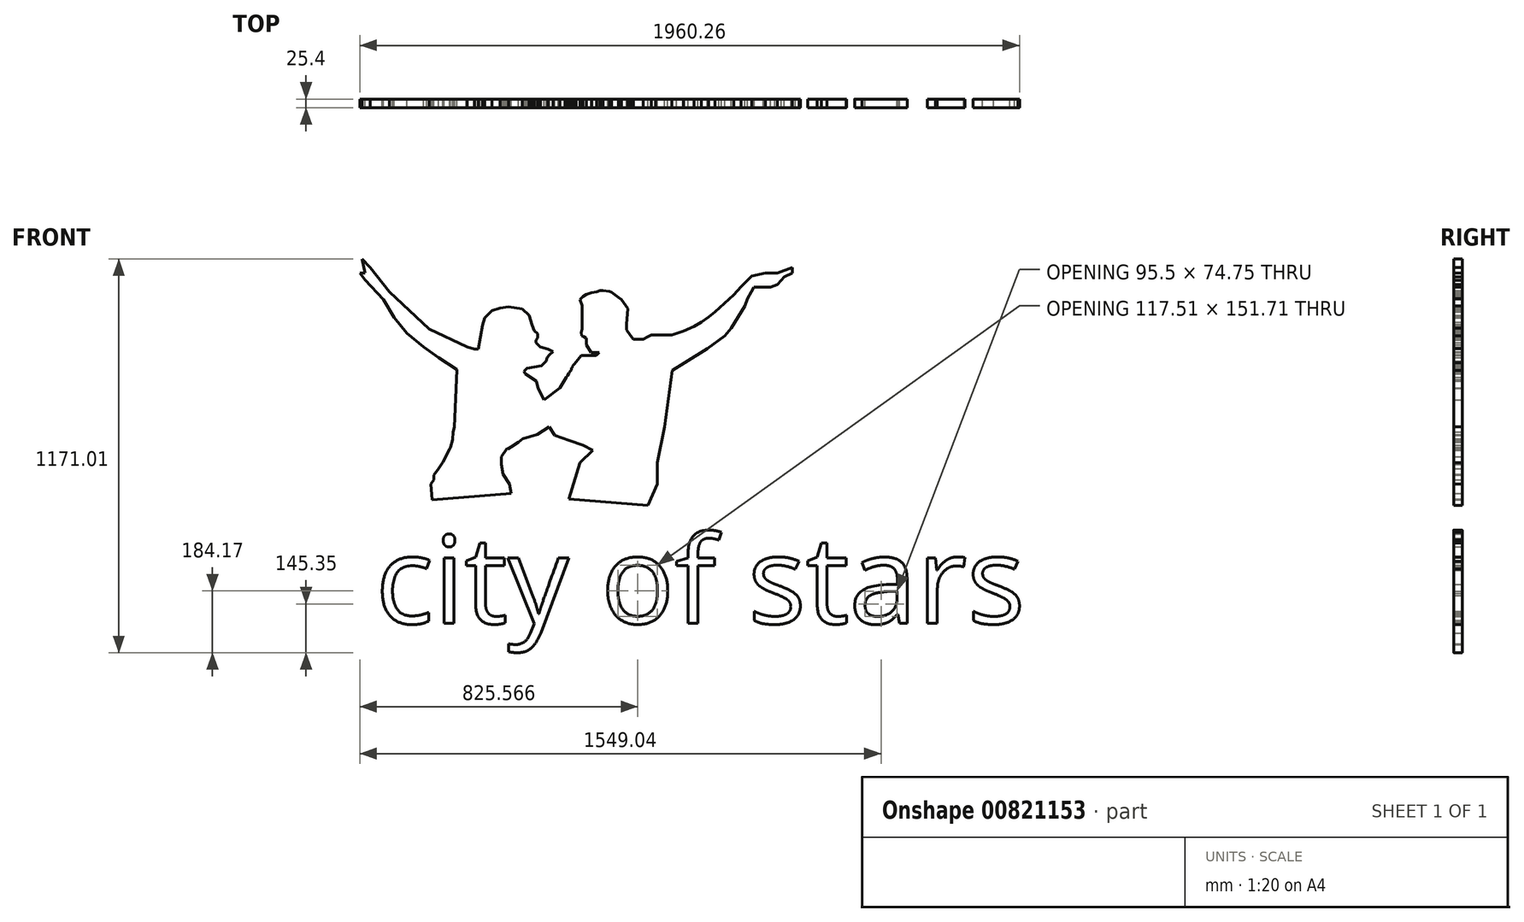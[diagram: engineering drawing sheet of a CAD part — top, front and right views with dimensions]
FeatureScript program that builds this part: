
annotation { "Feature Type Name" : "Feature", "Feature Type Description" : "" }
export const myFeature = defineFeature(function(context is Context, id is Id, definition is map)
    precondition{}
    {
        {
            var Q0;
            Q0=qCreatedBy(makeId("Front.planeOp"),FACE);
            var sketch = newSketch(context, id + "F0", { "sketchPlane" : qUnion([Q0])});
            skLineSegment(sketch, "E0", {"start": v(-24.6, -208.57) * mm, "end": v(-79.3, -173.4) * mm});
            skLineSegment(sketch, "E1", {"start": v(-79.3, -173.4) * mm, "end": v(-123.58, -142.15) * mm});
            skLineSegment(sketch, "E2", {"start": v(-123.58, -142.15) * mm, "end": v(-173.07, -100.48) * mm});
            skLineSegment(sketch, "E3", {"start": v(-173.07, -100.48) * mm, "end": v(-212.13, -53.6) * mm});
            skLineSegment(sketch, "E4", {"start": v(-212.13, -53.6) * mm, "end": v(-243.39, 0) * mm});
            skLineSegment(sketch, "E5", {"start": v(-243.39, 0) * mm, "end": v(-298.08, 58.4) * mm});
            skLineSegment(sketch, "E6", {"start": v(-298.08, 58.4) * mm, "end": v(-313.15, 78.62) * mm});
            skLineSegment(sketch, "E7", {"start": v(-313.15, 78.62) * mm, "end": v(-298.41, 78.62) * mm});
            skLineSegment(sketch, "E8", {"start": v(-298.41, 78.62) * mm, "end": v(-306.72, 120.17) * mm});
            skLineSegment(sketch, "E9", {"start": v(-306.72, 120.17) * mm, "end": v(-282.38, 94.19) * mm});
            skLineSegment(sketch, "E10", {"start": v(-282.38, 94.19) * mm, "end": v(-225.5, 22.33) * mm});
            skLineSegment(sketch, "E11", {"start": v(-225.5, 22.33) * mm, "end": v(-177.52, -22.63) * mm});
            skLineSegment(sketch, "E12", {"start": v(-177.52, -22.63) * mm, "end": v(-131.04, -66.18) * mm});
            skLineSegment(sketch, "E13", {"start": v(-131.04, -66.18) * mm, "end": v(-107.71, -88.04) * mm});
            skLineSegment(sketch, "E14", {"start": v(-107.71, -88.04) * mm, "end": v(4.94, -141.63) * mm});
            skLineSegment(sketch, "E15", {"start": v(4.94, -141.63) * mm, "end": v(26.85, -148.43) * mm});
            skLineSegment(sketch, "E16", {"start": v(26.85, -148.43) * mm, "end": v(38.19, -148.43) * mm});
            skLineSegment(sketch, "E17", {"start": v(38.19, -148.43) * mm, "end": v(51.4, -76.65) * mm});
            skLineSegment(sketch, "E18", {"start": v(51.4, -76.65) * mm, "end": v(58.06, -55.21) * mm});
            skLineSegment(sketch, "E19", {"start": v(58.06, -55.21) * mm, "end": v(78.67, -33.22) * mm});
            skLineSegment(sketch, "E20", {"start": v(78.67, -33.22) * mm, "end": v(102.79, -25.65) * mm});
            skLineSegment(sketch, "E21", {"start": v(102.79, -25.65) * mm, "end": v(128.88, -22.63) * mm});
            skLineSegment(sketch, "E22", {"start": v(128.88, -22.63) * mm, "end": v(168.72, -28.06) * mm});
            skLineSegment(sketch, "E23", {"start": v(168.72, -28.06) * mm, "end": v(189.58, -47.6) * mm});
            skLineSegment(sketch, "E24", {"start": v(189.58, -47.6) * mm, "end": v(198.86, -76.65) * mm});
            skLineSegment(sketch, "E25", {"start": v(198.86, -76.65) * mm, "end": v(205, -92.93) * mm});
            skLineSegment(sketch, "E26", {"start": v(205, -92.93) * mm, "end": v(215.26, -102.55) * mm});
            skLineSegment(sketch, "E27", {"start": v(215.26, -102.55) * mm, "end": v(215.26, -115.4) * mm});
            skLineSegment(sketch, "E28", {"start": v(215.26, -115.4) * mm, "end": v(209.33, -120.96) * mm});
            skLineSegment(sketch, "E29", {"start": v(209.33, -120.96) * mm, "end": v(209.33, -129.2) * mm});
            skLineSegment(sketch, "E30", {"start": v(209.33, -129.2) * mm, "end": v(222.04, -141.11) * mm});
            skLineSegment(sketch, "E31", {"start": v(222.04, -141.11) * mm, "end": v(245.6, -148.43) * mm});
            skLineSegment(sketch, "E32", {"start": v(245.6, -148.43) * mm, "end": v(260.68, -155.6) * mm});
            skLineSegment(sketch, "E33", {"start": v(260.68, -155.6) * mm, "end": v(251, -164.66) * mm});
            skLineSegment(sketch, "E34", {"start": v(251, -164.66) * mm, "end": v(243.5, -172.67) * mm});
            skLineSegment(sketch, "E35", {"start": v(243.5, -172.67) * mm, "end": v(240.24, -182.84) * mm});
            skLineSegment(sketch, "E36", {"start": v(240.24, -182.84) * mm, "end": v(226.73, -197.25) * mm});
            skLineSegment(sketch, "E37", {"start": v(226.73, -197.25) * mm, "end": v(183.54, -204.8) * mm});
            skLineSegment(sketch, "E38", {"start": v(183.54, -204.8) * mm, "end": v(174.41, -214.54) * mm});
            skLineSegment(sketch, "E39", {"start": v(174.41, -214.54) * mm, "end": v(178.43, -221.66) * mm});
            skLineSegment(sketch, "E40", {"start": v(178.43, -221.66) * mm, "end": v(211.63, -243.62) * mm});
            skLineSegment(sketch, "E41", {"start": v(211.63, -243.62) * mm, "end": v(216.23, -264.57) * mm});
            skLineSegment(sketch, "E42", {"start": v(216.23, -264.57) * mm, "end": v(234.62, -298.8) * mm});
            skLineSegment(sketch, "E43", {"start": v(234.62, -298.8) * mm, "end": v(280.6, -264.06) * mm});
            skLineSegment(sketch, "E44", {"start": v(280.6, -264.06) * mm, "end": v(296.94, -238) * mm});
            skLineSegment(sketch, "E45", {"start": v(296.94, -238) * mm, "end": v(300, -231.87) * mm});
            skLineSegment(sketch, "E46", {"start": v(300, -231.87) * mm, "end": v(303.58, -226.26) * mm});
            skLineSegment(sketch, "E47", {"start": v(303.58, -226.26) * mm, "end": v(307.15, -220.64) * mm});
            skLineSegment(sketch, "E48", {"start": v(307.15, -220.64) * mm, "end": v(309.2, -217.57) * mm});
            skLineSegment(sketch, "E49", {"start": v(309.2, -217.57) * mm, "end": v(311.75, -213.49) * mm});
            skLineSegment(sketch, "E50", {"start": v(311.75, -213.49) * mm, "end": v(314.82, -209.9) * mm});
            skLineSegment(sketch, "E51", {"start": v(314.82, -209.9) * mm, "end": v(314.82, -203.27) * mm});
            skLineSegment(sketch, "E52", {"start": v(314.82, -203.27) * mm, "end": v(317.37, -203.27) * mm});
            skLineSegment(sketch, "E53", {"start": v(318.4, -199.7) * mm, "end": v(321.97, -195.1) * mm});
            skLineSegment(sketch, "E54", {"start": v(321.97, -195.1) * mm, "end": v(324.01, -192.54) * mm});
            skLineSegment(sketch, "E55", {"start": v(324.01, -192.54) * mm, "end": v(329.12, -185.4) * mm});
            skLineSegment(sketch, "E56", {"start": v(329.12, -185.4) * mm, "end": v(344.95, -167.51) * mm});
            skLineSegment(sketch, "E57", {"start": v(344.95, -167.51) * mm, "end": v(388.56, -167.51) * mm});
            skLineSegment(sketch, "E58", {"start": v(388.56, -167.51) * mm, "end": v(397.42, -158.06) * mm});
            skLineSegment(sketch, "E59", {"start": v(397.42, -158.06) * mm, "end": v(373.8, -158.06) * mm});
            skLineSegment(sketch, "E60", {"start": v(373.8, -158.06) * mm, "end": v(359.75, -134.75) * mm});
            skLineSegment(sketch, "E61", {"start": v(359.75, -134.75) * mm, "end": v(359.75, -118.95) * mm});
            skLineSegment(sketch, "E62", {"start": v(359.75, -118.95) * mm, "end": v(358.48, -114.43) * mm});
            skLineSegment(sketch, "E63", {"start": v(358.48, -114.43) * mm, "end": v(352.73, -111.28) * mm});
            skLineSegment(sketch, "E64", {"start": v(346.35, -108.57) * mm, "end": v(344.95, -97.73) * mm});
            skLineSegment(sketch, "E65", {"start": v(344.95, -97.73) * mm, "end": v(346.99, -87.8) * mm});
            skLineSegment(sketch, "E66", {"start": v(346.99, -87.8) * mm, "end": v(346.99, -61.17) * mm});
            skLineSegment(sketch, "E67", {"start": v(352.73, -111.28) * mm, "end": v(346.35, -108.57) * mm});
            skLineSegment(sketch, "E68", {"start": v(346.99, -61.17) * mm, "end": v(346.99, -34) * mm});
            skLineSegment(sketch, "E69", {"start": v(346.99, -34) * mm, "end": v(346.99, -18.52) * mm});
            skLineSegment(sketch, "E70", {"start": v(346.99, -18.52) * mm, "end": v(341.37, 0) * mm});
            skLineSegment(sketch, "E71", {"start": v(341.37, 0) * mm, "end": v(350.3, 7.7) * mm});
            skLineSegment(sketch, "E72", {"start": v(350.3, 7.7) * mm, "end": v(360.05, 14.94) * mm});
            skLineSegment(sketch, "E73", {"start": v(360.05, 14.94) * mm, "end": v(375, 20.23) * mm});
            skLineSegment(sketch, "E74", {"start": v(375, 20.23) * mm, "end": v(389.68, 22.88) * mm});
            skLineSegment(sketch, "E75", {"start": v(389.68, 22.88) * mm, "end": v(400.6, 25.52) * mm});
            skLineSegment(sketch, "E76", {"start": v(400.6, 25.52) * mm, "end": v(404.92, 26.13) * mm});
            skLineSegment(sketch, "E77", {"start": v(404.92, 26.13) * mm, "end": v(409.24, 26.13) * mm});
            skLineSegment(sketch, "E78", {"start": v(409.24, 26.13) * mm, "end": v(428.22, 23.7) * mm});
            skLineSegment(sketch, "E79", {"start": v(428.22, 23.7) * mm, "end": v(434.84, 21.25) * mm});
            skLineSegment(sketch, "E80", {"start": v(434.84, 21.25) * mm, "end": v(454.69, 5.59) * mm});
            skLineSegment(sketch, "E81", {"start": v(454.69, 5.59) * mm, "end": v(464.18, -0.1) * mm});
            skLineSegment(sketch, "E82", {"start": v(464.18, -0.1) * mm, "end": v(482.59, -27.77) * mm});
            skLineSegment(sketch, "E83", {"start": v(482.59, -27.77) * mm, "end": v(479.14, -74.15) * mm});
            skLineSegment(sketch, "E84", {"start": v(479.14, -74.15) * mm, "end": v(479.14, -91.15) * mm});
            skLineSegment(sketch, "E85", {"start": v(479.14, -91.15) * mm, "end": v(490, -106.9) * mm});
            skLineSegment(sketch, "E86", {"start": v(490, -106.9) * mm, "end": v(498.9, -118.11) * mm});
            skLineSegment(sketch, "E87", {"start": v(498.9, -118.11) * mm, "end": v(529.23, -118.11) * mm});
            skLineSegment(sketch, "E88", {"start": v(529.23, -118.11) * mm, "end": v(543.15, -111.03) * mm});
            skLineSegment(sketch, "E89", {"start": v(543.15, -111.03) * mm, "end": v(553.44, -105.72) * mm});
            skLineSegment(sketch, "E90", {"start": v(553.44, -105.72) * mm, "end": v(565.68, -106.11) * mm});
            skLineSegment(sketch, "E91", {"start": v(565.68, -106.11) * mm, "end": v(613.7, -106.11) * mm});
            skLineSegment(sketch, "E92", {"start": v(613.7, -106.11) * mm, "end": v(648.53, -93.94) * mm});
            skLineSegment(sketch, "E93", {"start": v(648.53, -93.94) * mm, "end": v(680.26, -80.8) * mm});
            skLineSegment(sketch, "E94", {"start": v(680.26, -80.8) * mm, "end": v(701.15, -68.22) * mm});
            skLineSegment(sketch, "E95", {"start": v(701.15, -68.22) * mm, "end": v(723.6, -52.9) * mm});
            skLineSegment(sketch, "E96", {"start": v(723.6, -52.9) * mm, "end": v(742.17, -37.03) * mm});
            skLineSegment(sketch, "E97", {"start": v(742.17, -37.03) * mm, "end": v(797.89, 13.31) * mm});
            skLineSegment(sketch, "E98", {"start": v(797.89, 13.31) * mm, "end": v(819.55, 37.39) * mm});
            skLineSegment(sketch, "E99", {"start": v(819.55, 37.39) * mm, "end": v(851.28, 69.67) * mm});
            skLineSegment(sketch, "E100", {"start": v(851.28, 69.67) * mm, "end": v(891.52, 77.88) * mm});
            skLineSegment(sketch, "E101", {"start": v(891.52, 77.88) * mm, "end": v(927.12, 77.88) * mm});
            skLineSegment(sketch, "E102", {"start": v(927.12, 77.88) * mm, "end": v(972, 94.84) * mm});
            skLineSegment(sketch, "E103", {"start": v(972, 94.84) * mm, "end": v(972, 77.88) * mm});
            skLineSegment(sketch, "E104", {"start": v(972, 77.88) * mm, "end": v(947.24, 66.39) * mm});
            skLineSegment(sketch, "E105", {"start": v(947.24, 66.39) * mm, "end": v(938.73, 56) * mm});
            skLineSegment(sketch, "E106", {"start": v(938.73, 56) * mm, "end": v(927.12, 44.5) * mm});
            skLineSegment(sketch, "E107", {"start": v(927.12, 44.5) * mm, "end": v(907, 36.84) * mm});
            skLineSegment(sketch, "E108", {"start": v(907, 36.84) * mm, "end": v(857.47, 36.84) * mm});
            skLineSegment(sketch, "E109", {"start": v(857.47, 36.84) * mm, "end": v(849.74, 22.07) * mm});
            skLineSegment(sketch, "E110", {"start": v(849.74, 22.07) * mm, "end": v(838.9, 1.82) * mm});
            skLineSegment(sketch, "E111", {"start": v(838.9, 1.82) * mm, "end": v(830.39, -18.98) * mm});
            skLineSegment(sketch, "E112", {"start": v(830.39, -18.98) * mm, "end": v(790.15, -85.73) * mm});
            skLineSegment(sketch, "E113", {"start": v(790.15, -85.73) * mm, "end": v(770.8, -108.72) * mm});
            skLineSegment(sketch, "E114", {"start": v(770.8, -108.72) * mm, "end": v(719.72, -147.02) * mm});
            skLineSegment(sketch, "E115", {"start": v(719.72, -147.02) * mm, "end": v(651.62, -188.61) * mm});
            skLineSegment(sketch, "E116", {"start": v(651.62, -188.61) * mm, "end": v(631.5, -201.2) * mm});
            skLineSegment(sketch, "E117", {"start": v(631.5, -201.2) * mm, "end": v(614.78, -211.65) * mm});
            skLineSegment(sketch, "E118", {"start": v(614.78, -211.65) * mm, "end": v(592.04, -379.59) * mm});
            skLineSegment(sketch, "E119", {"start": v(592.04, -379.59) * mm, "end": v(571.14, -485.2) * mm});
            skLineSegment(sketch, "E120", {"start": v(571.14, -485.2) * mm, "end": v(571.14, -548.62) * mm});
            skLineSegment(sketch, "E121", {"start": v(571.14, -548.62) * mm, "end": v(542.3, -612.08) * mm});
            skLineSegment(sketch, "E122", {"start": v(542.3, -612.08) * mm, "end": v(308.03, -593.8) * mm});
            skLineSegment(sketch, "E123", {"start": v(308.03, -593.8) * mm, "end": v(340.74, -485.2) * mm});
            skLineSegment(sketch, "E124", {"start": v(340.74, -485.2) * mm, "end": v(378.77, -448.59) * mm});
            skLineSegment(sketch, "E125", {"start": v(378.77, -448.59) * mm, "end": v(350.3, -434.07) * mm});
            skLineSegment(sketch, "E126", {"start": v(350.3, -434.07) * mm, "end": v(308.8, -419.55) * mm});
            skLineSegment(sketch, "E127", {"start": v(308.8, -419.55) * mm, "end": v(265.44, -405.03) * mm});
            skLineSegment(sketch, "E128", {"start": v(265.44, -405.03) * mm, "end": v(249.53, -379.59) * mm});
            skLineSegment(sketch, "E129", {"start": v(249.53, -379.59) * mm, "end": v(213.56, -402.08) * mm});
            skLineSegment(sketch, "E130", {"start": v(213.56, -402.08) * mm, "end": v(171.13, -414.7) * mm});
            skLineSegment(sketch, "E131", {"start": v(171.13, -414.7) * mm, "end": v(158.2, -424.93) * mm});
            skLineSegment(sketch, "E132", {"start": v(158.2, -424.93) * mm, "end": v(135.7, -439) * mm});
            skLineSegment(sketch, "E133", {"start": v(135.7, -439) * mm, "end": v(126.26, -444.82) * mm});
            skLineSegment(sketch, "E134", {"start": v(126.26, -444.82) * mm, "end": v(123.21, -443.75) * mm});
            skLineSegment(sketch, "E135", {"start": v(123.21, -443.75) * mm, "end": v(107.24, -467.95) * mm});
            skLineSegment(sketch, "E136", {"start": v(107.24, -467.95) * mm, "end": v(107.24, -491.08) * mm});
            skLineSegment(sketch, "E137", {"start": v(107.24, -491.08) * mm, "end": v(112.68, -519.39) * mm});
            skLineSegment(sketch, "E138", {"start": v(112.68, -519.39) * mm, "end": v(131.29, -549.13) * mm});
            skLineSegment(sketch, "E139", {"start": v(131.29, -549.13) * mm, "end": v(136.23, -576.73) * mm});
            skLineSegment(sketch, "E140", {"start": v(136.23, -576.73) * mm, "end": v(-98.5, -596.66) * mm});
            skLineSegment(sketch, "E141", {"start": v(-98.5, -596.66) * mm, "end": v(-102.54, -549.13) * mm});
            skLineSegment(sketch, "E142", {"start": v(-102.54, -549.13) * mm, "end": v(-93.56, -536.85) * mm});
            skLineSegment(sketch, "E143", {"start": v(-93.56, -536.85) * mm, "end": v(-93.56, -521.9) * mm});
            skLineSegment(sketch, "E144", {"start": v(-93.56, -521.9) * mm, "end": v(-79.47, -503.46) * mm});
            skLineSegment(sketch, "E145", {"start": v(-79.47, -503.46) * mm, "end": v(-67.48, -484.52) * mm});
            skLineSegment(sketch, "E146", {"start": v(-67.48, -484.52) * mm, "end": v(-46.34, -444.64) * mm});
            skLineSegment(sketch, "E147", {"start": v(-43.52, -440.16) * mm, "end": v(-37.17, -417.23) * mm});
            skLineSegment(sketch, "E148", {"start": v(-37.17, -417.23) * mm, "end": v(-36.47, -393.8) * mm});
            skLineSegment(sketch, "E149", {"start": v(-36.47, -393.8) * mm, "end": v(-32.24, -379.85) * mm});
            skLineSegment(sketch, "E150", {"start": v(-43.52, -440.16) * mm, "end": v(-46.34, -444.64) * mm});
            skLineSegment(sketch, "E151", {"start": v(-32.24, -379.85) * mm, "end": v(-24.6, -208.57) * mm});
            skLineSegment(sketch, "E152", {"start": v(317.37, -203.27) * mm, "end": v(318.4, -199.7) * mm});
            skSolve(sketch);
        }
        {
            var Q0;
            Q0 = qSketchRegion(id + "F0", true);
            extrude(context, id + "F1", {"entities" : qUnion([Q0]), "depth" : 25.4 * mm, "offsetDistance" : 25.4 * mm});
        }
        {
            var Q0;
            Q0=qCreatedBy(makeId("Front.planeOp"),FACE);
            var sketch = newSketch(context, id + "F2", { "sketchPlane" : qUnion([Q0])});
            skText(sketch, "E153", { "text": "city of stars\n", "fontName": "OpenSans-Regular.ttf"});
            const initialGuessF2  = {"E153": [-0.26715, -0.96362, 1, 0, 0.26133]};
            skSetInitialGuess(sketch, initialGuessF2);
            skSolve(sketch);
        }
        {
            var Q0;
            Q0 = qSketchRegion(id + "F2", true);
            extrude(context, id + "F3", {"entities" : qUnion([Q0]), "depth" : 25.4 * mm, "offsetDistance" : 25.4 * mm});
        }
    });
